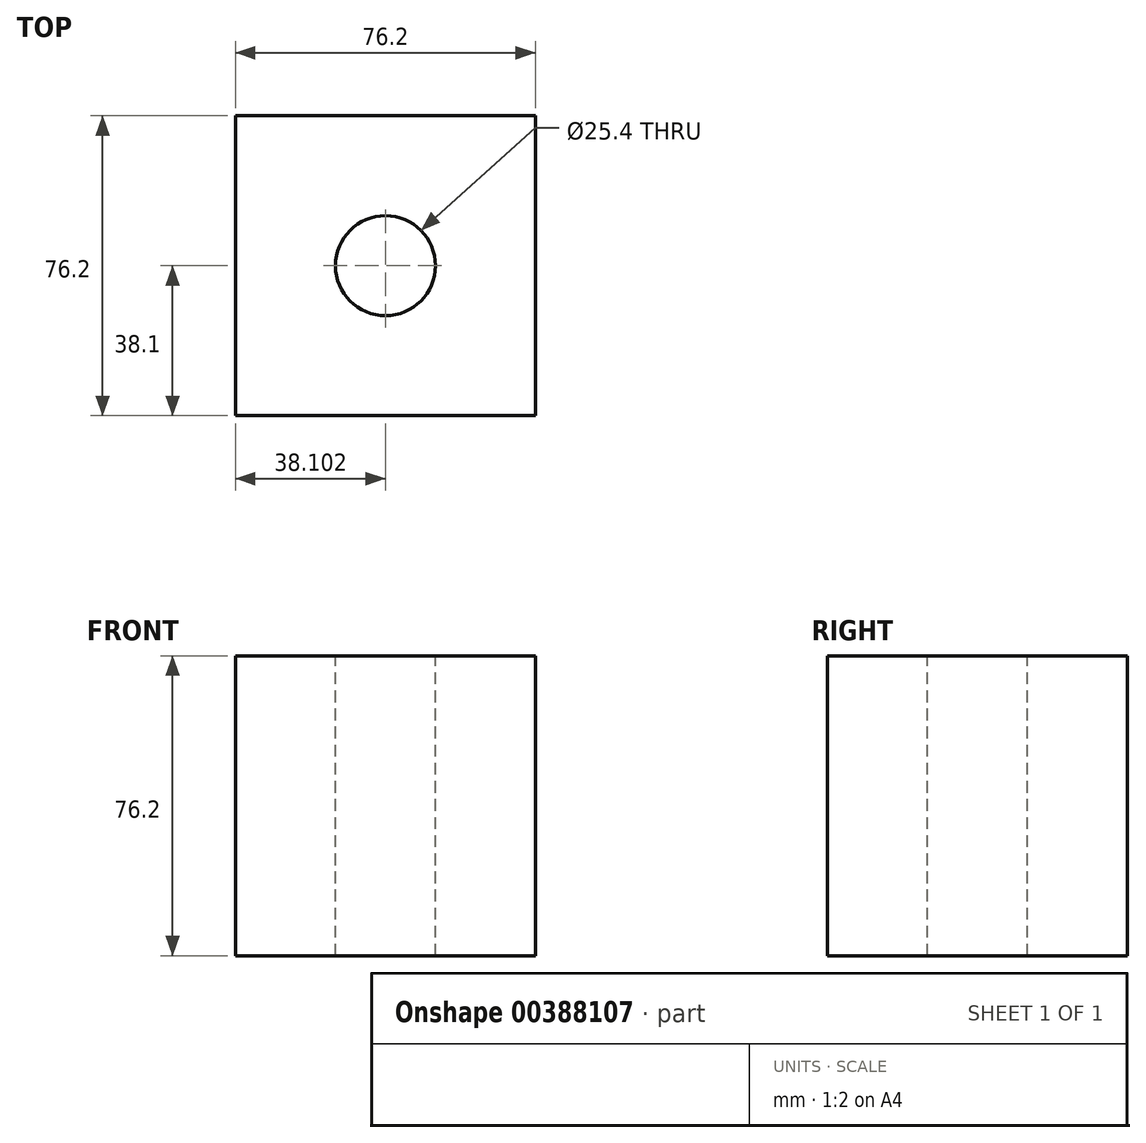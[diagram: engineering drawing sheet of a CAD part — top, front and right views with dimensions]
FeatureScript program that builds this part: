
annotation { "Feature Type Name" : "Feature", "Feature Type Description" : "" }
export const myFeature = defineFeature(function(context is Context, id is Id, definition is map)
    precondition{}
    {
        {
            var Q0;
            Q0=qCreatedBy(makeId("Front.planeOp"),FACE);
            var sketch = newSketch(context, id + "F0", { "sketchPlane" : qUnion([Q0])});
            skLineSegment(sketch, "E0.bottom", {"start": v(-27.75, 32.4) * mm, "end": v(48.45, 32.4) * mm});
            skLineSegment(sketch, "E0.top", {"start": v(-27.75, -43.8) * mm, "end": v(48.45, -43.8) * mm});
            skLineSegment(sketch, "E0.left", {"start": v(-27.75, 32.4) * mm, "end": v(-27.75, -43.8) * mm});
            skLineSegment(sketch, "E0.right", {"start": v(48.45, 32.4) * mm, "end": v(48.45, -43.8) * mm});
            skSolve(sketch);
        }
        {
            var Q0;
            Q0=makeQuery(id+"F0.imprint","IMPRINT",FACE,{"disambiguationData":[TD([[makeQuery(id+"F0.imprint","IMPRINT",EDGE,{"derivedFrom":sQuery(id+"F0.wireOp",EDGE,"E0.bottom")}),-1.0]])]});
            extrude(context, id + "F1", {"entities" : qUnion([Q0]), "depth" : 76.2 * mm});
        }
        {
            var Q0;
            Q0=makeQuery(id+"F1.opExtrude","SWEPT_FACE",FACE,{"disambiguationData":[OSD([sQuery(id+"F0.wireOp",EDGE,"E0.bottom")])]});
            var sketch = newSketch(context, id + "F2", { "sketchPlane" : qUnion([Q0])});
            skPoint(sketch, "E1", {"position": v(10.35, -38.1) * mm});
            skSolve(sketch);
        }
        {
            var Q0;
            Q0=sQuery(id+"F2.wireOp",VERTEX,"E1");
            var Q1;
            Q1=makeQuery(id+"F1.opExtrude","SWEPT_BODY",BODY,{"disambiguationData":[OSD([sQuery(id+"F0.wireOp",EDGE,"E0.bottom"),sQuery(id+"F0.wireOp",EDGE,"E0.top"),sQuery(id+"F0.wireOp",EDGE,"E0.left"),sQuery(id+"F0.wireOp",EDGE,"E0.right")])]});
            hole(context, id + "F3", {"style" : HoleStyle.SIMPLE, "endStyle" : HoleEndStyle.THROUGH, "holeDiameter" : 25.4 * mm, "isTappedThrough" : true, "tappedDepth" : 12.7 * mm, "tapClearance" : 3, "locations" : qUnion([Q0]), "scope" : qUnion([Q1])});
        }
    });
